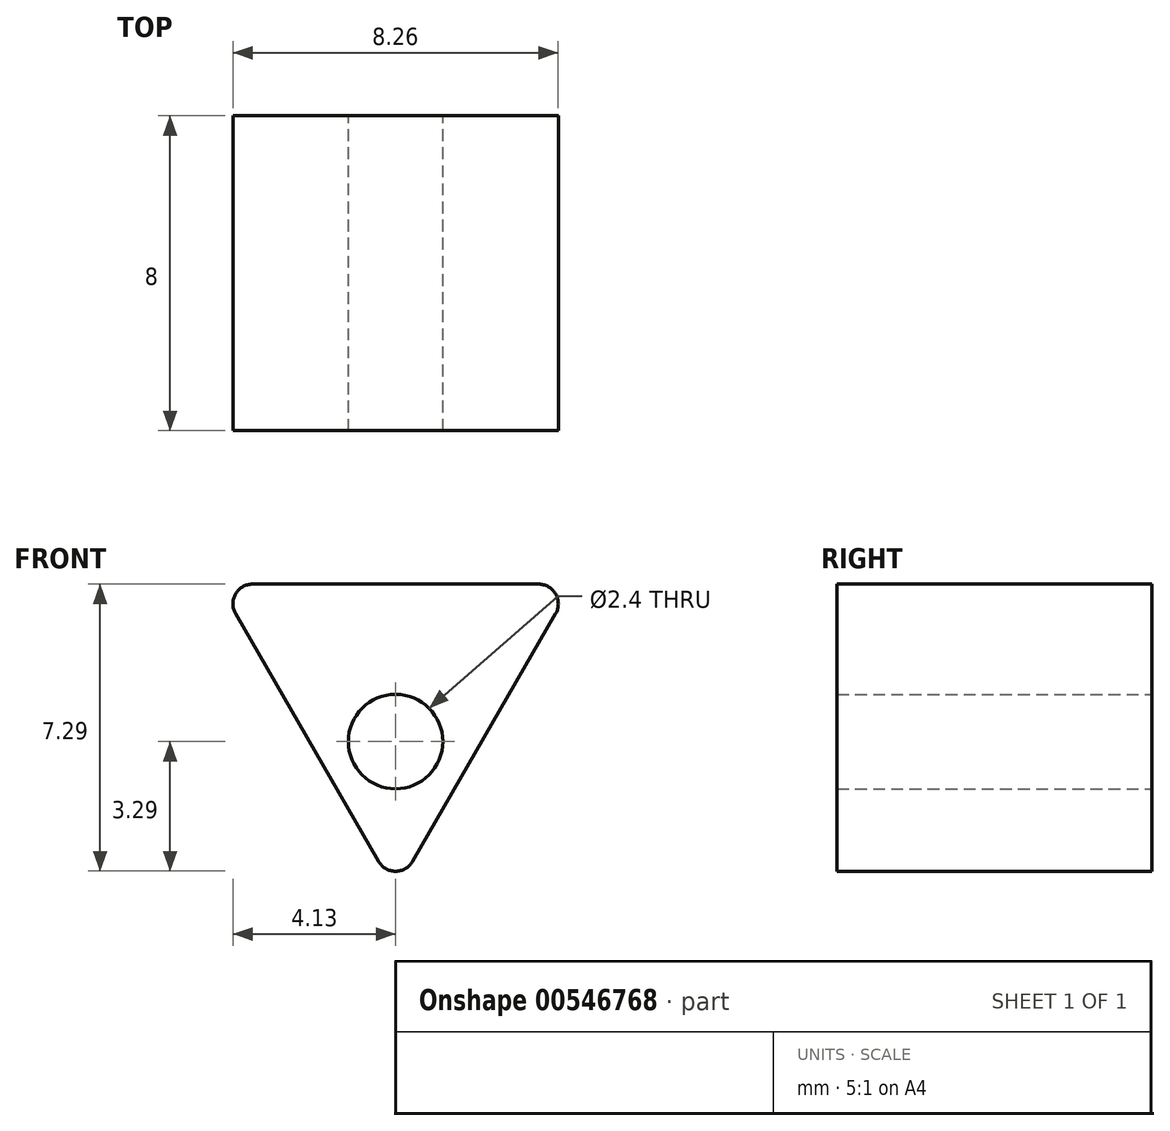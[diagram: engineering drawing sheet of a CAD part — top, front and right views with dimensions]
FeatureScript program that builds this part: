
annotation { "Feature Type Name" : "Feature", "Feature Type Description" : "" }
export const myFeature = defineFeature(function(context is Context, id is Id, definition is map)
    precondition{}
    {
        {
            var Q0;
            Q0=qCreatedBy(makeId("Front.planeOp"),FACE);
            var sketch = newSketch(context, id + "F0", { "sketchPlane" : qUnion([Q0])});
            skLineSegment(sketch, "E0", {"start": v(-3.63, 0) * mm, "end": v(3.63, 0) * mm});
            skPoint(sketch, "E1", {"position": v(0, 0) * mm});
            skLineSegment(sketch, "E2", {"start": v(-4.07, -0.75) * mm, "end": v(-0.43, -7.04) * mm});
            skLineSegment(sketch, "E3", {"start": v(0.43, -7.04) * mm, "end": v(4.07, -0.75) * mm});
            skPoint(sketch, "E4.visualSharp", {"position": v(-4.5, 0) * mm});
            skArc(sketch, "E4.filletArc", {"start": v(-3.63, 0) * mm, "mid": v(-4.07, -0.25) * mm, "end": v(-4.07, -0.75) * mm});
            skPoint(sketch, "E5.visualSharp", {"position": v(4.5, 0) * mm});
            skArc(sketch, "E5.filletArc", {"start": v(4.07, -0.75) * mm, "mid": v(4.07, -0.25) * mm, "end": v(3.63, 0) * mm});
            skPoint(sketch, "E6.visualSharp", {"position": v(0, -7.8) * mm});
            skArc(sketch, "E6.filletArc", {"start": v(-0.43, -7.04) * mm, "mid": v(0, -7.3) * mm, "end": v(0.43, -7.04) * mm});
            skCircle(sketch, "E7", {"center": v(0, -4) * mm, "radius": 1.2 * mm});
            skSolve(sketch);
        }
        {
            var Q0;
            Q0 = qSketchRegion(id + "F0", true);
            extrude(context, id + "F1", {"entities" : qUnion([Q0]), "depth" : 8 * mm, "offsetDistance" : 25 * mm});
        }
    });
